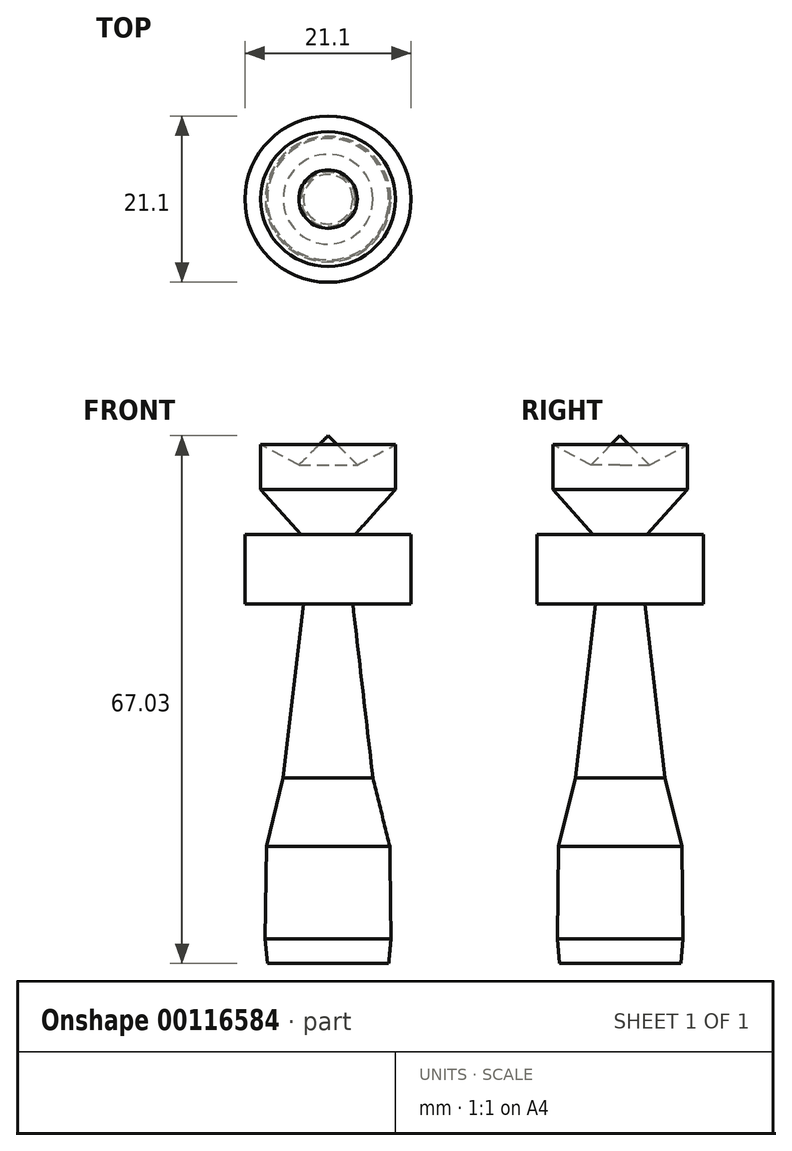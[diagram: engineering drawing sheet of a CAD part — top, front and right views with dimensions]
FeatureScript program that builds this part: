
annotation { "Feature Type Name" : "Feature", "Feature Type Description" : "" }
export const myFeature = defineFeature(function(context is Context, id is Id, definition is map)
    precondition{}
    {
        {
            var Q0;
            Q0=qCreatedBy(makeId("Front.planeOp"),FACE);
            var sketch = newSketch(context, id + "F0", { "sketchPlane" : qUnion([Q0])});
            skLineSegment(sketch, "E0", {"start": v(0, -20.4) * mm, "end": v(-7.99, -20.4) * mm});
            skLineSegment(sketch, "E1", {"start": v(-7.99, -20.4) * mm, "end": v(-7.7, -23.53) * mm});
            skLineSegment(sketch, "E2", {"start": v(-7.99, -20.4) * mm, "end": v(-7.84, -8.7) * mm});
            skPoint(sketch, "E2.endSnap0", {"position": v(-7.84, -21.96) * mm});
            skLineSegment(sketch, "E3", {"start": v(-7.84, -8.7) * mm, "end": v(-5.7, 0) * mm});
            skLineSegment(sketch, "E4", {"start": v(-5.7, 0) * mm, "end": v(-3.14, 22.1) * mm});
            skLineSegment(sketch, "E5", {"start": v(-3.14, 22.1) * mm, "end": v(-10.55, 22.1) * mm});
            skLineSegment(sketch, "E6", {"start": v(-10.55, 22.1) * mm, "end": v(-10.55, 30.95) * mm});
            skLineSegment(sketch, "E7", {"start": v(-8.56, 36.65) * mm, "end": v(-8.56, 42.36) * mm});
            skPoint(sketch, "E8.end.orphan", {"position": v(0, 43.5) * mm});
            skPoint(sketch, "E9.start.orphan", {"position": v(0, 30.95) * mm});
            skLineSegment(sketch, "E10", {"start": v(-10.55, 30.95) * mm, "end": v(-3.42, 30.95) * mm});
            skLineSegment(sketch, "E11", {"start": v(-3.42, 30.95) * mm, "end": v(-8.56, 36.65) * mm});
            skLineSegment(sketch, "E12", {"start": v(-8.56, 42.36) * mm, "end": v(-3.7, 39.8) * mm});
            skLineSegment(sketch, "E13", {"start": v(-3.7, 39.8) * mm, "end": v(0, 43.5) * mm});
            skLineSegment(sketch, "E14", {"start": v(0, 43.5) * mm, "end": v(0, 30.95) * mm});
            skLineSegment(sketch, "E15", {"start": v(-7.7, -23.53) * mm, "end": v(0, -23.53) * mm});
            skLineSegment(sketch, "E16", {"start": v(0, 43.5) * mm, "end": v(0, -23.53) * mm});
            skSolve(sketch);
        }
        {
            var Q0;
            Q0 = qSketchRegion(id + "F0", true);
            var Q1;
            Q1=sQuery(id+"F0.wireOp",EDGE,"E16");
            revolve(context, id + "F1", {"entities" : qUnion([Q0]), "axis" : qUnion([Q1]), "revolveType" : RevolveType.FULL});
        }
    });
